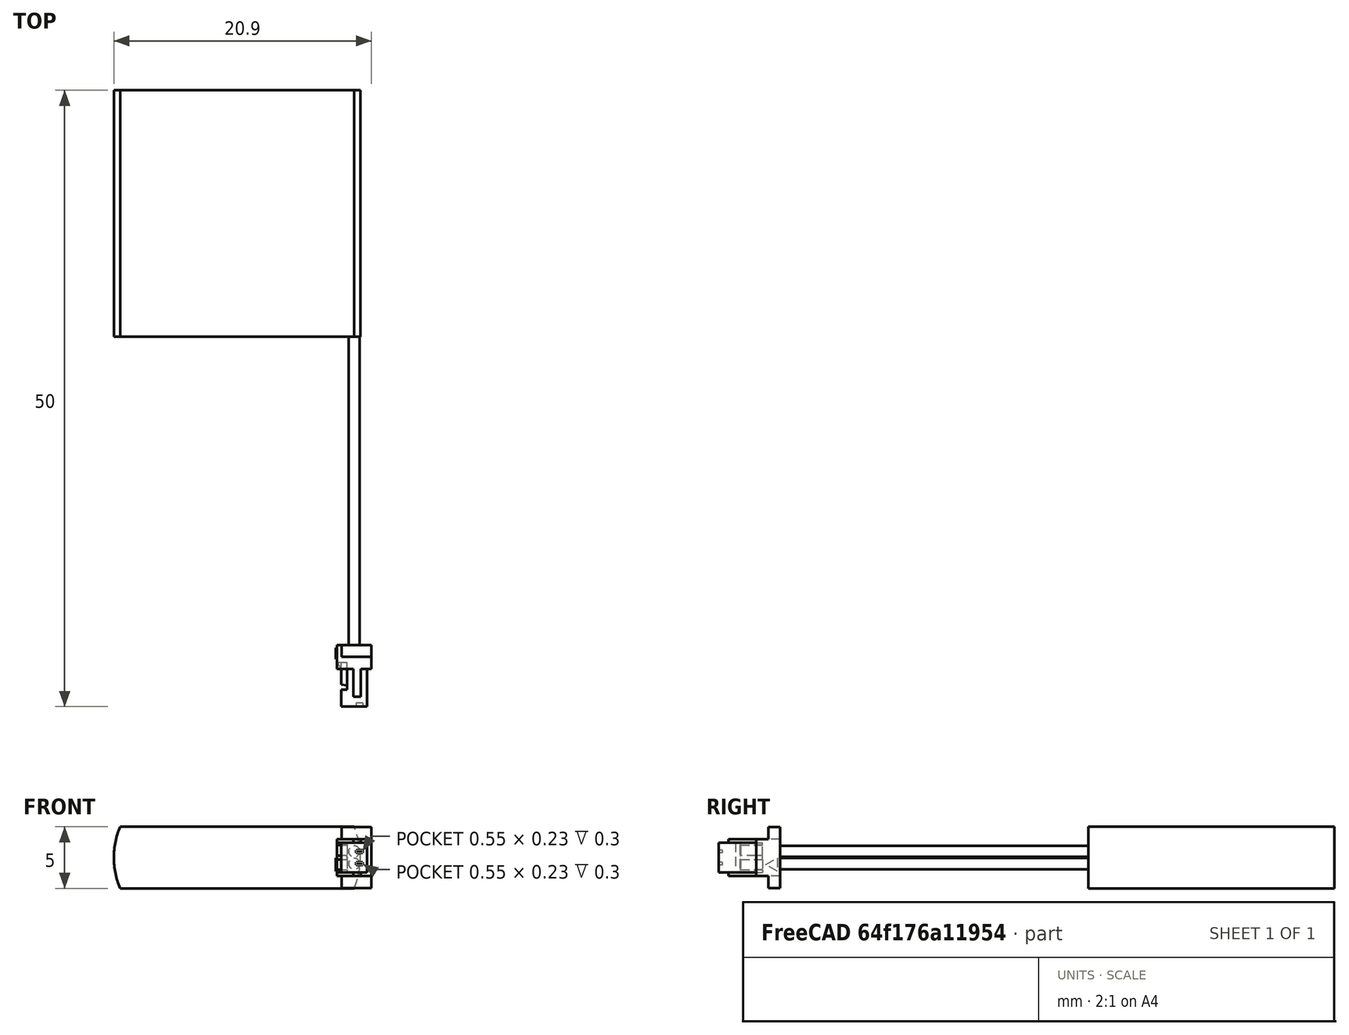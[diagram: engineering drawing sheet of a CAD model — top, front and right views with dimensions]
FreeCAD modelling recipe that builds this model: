
FCSTD DOCUMENT  (FreeCAD 2021.519R24301 +3652 (Git))
Label: ASR00003_150mAh
License: Other
objects: TechDraw::DrawViewDimension×4, Sketcher::SketchObject×3, PartDesign::Pad×3, TechDraw::DrawViewPart×2, TechDraw::DrawViewAnnotation×2, PartDesign::Pocket×1, PartDesign::Mirrored×1, PartDesign::Body×1, Part::Feature×1, Part::MultiFuse×1, TechDraw::DrawSVGTemplate×1, TechDraw::DrawPage×1, Mesh::Feature×1
note: 21 computed .brp shape members not serialized (recipe doc carries the construction recipe); baked Part::Feature solids carry a one-line shape summary decoded from their .brp

FEATURE [Sketcher::SketchObject] Sketch
  FullyConstrained = true
  MapMode = 5
  Support = -> [XY_Plane]
  sketch-geometry (4):
    g0: LineSegment StartX=-10 StartY=10 StartZ=0 EndX=10 EndY=10 EndZ=0
    g1: LineSegment StartX=10 StartY=10 StartZ=0 EndX=10 EndY=-10 EndZ=0
    g2: LineSegment StartX=10 StartY=-10 StartZ=0 EndX=-10 EndY=-10 EndZ=0
    g3: LineSegment StartX=-10 StartY=-10 StartZ=0 EndX=-10 EndY=10 EndZ=0
  constraints (10):
    c: Coincident(g0,g1)
    c: Coincident(g1,g2)
    c: Coincident(g2,g3)
    c: Coincident(g3,g0)
    c: Horizontal(g2)
    c: Vertical(g1)
    c: Symmetric(g0,g2,g-1)
    c: Symmetric(g0,g0,g-2)
    c: DistanceX(g0,g0) = 20
    c: DistanceY(g3,g3) = 20
FEATURE [PartDesign::Pad] Pad
  ClaimChildren = false
  Direction = (1,1,1)
  Fit = 0
  FitJoin = 0
  InnerFit = 0
  InnerFitJoin = 0
  InnerTaperAngle = 0
  InnerTaperAngleRev = 0
  Length = 5
  Length2 = 100
  Midplane = true
  NewSolid = false
  Profile = -> Sketch
  Suppress = false
  Type = 0
FEATURE [Sketcher::SketchObject] Sketch001
  ExternalGeometry = -> [Pad]
  FullyConstrained = true
  MapMode = 5
  Placement = pos=(0,10,0) rot=(0,0.707107,0.707107;3.14159rad)
  Support = -> [Pad]
  sketch-geometry (5):
    g0: ArcOfCircle CenterX=-3.5 CenterY=5e-16 CenterZ=0 NormalX=0 NormalY=0 NormalZ=1 AngleXU=0 Radius=6.5 StartAngle=2.7468 EndAngle=3.53638
    g1: LineSegment [constr] StartX=-9.5 StartY=-2.5 StartZ=0 EndX=-9.5 EndY=2.5 EndZ=0
    g2: LineSegment StartX=-9.5 StartY=-2.5 StartZ=0 EndX=-11 EndY=-2.5 EndZ=0
    g3: LineSegment StartX=-9.5 StartY=2.5 StartZ=0 EndX=-11 EndY=2.5 EndZ=0
    g4: LineSegment StartX=-11 StartY=2.5 StartZ=0 EndX=-11 EndY=-2.5 EndZ=0
  constraints (15):
    c: PointOnObject(g0,g-5)
    c: PointOnObject(g0,g-4)
    c: Tangent(g0,g-3)
    c: Coincident(g1,g0)
    c: Coincident(g1,g0)
    c: Vertical(g1)
    c: Coincident(g2,g0)
    c: Horizontal(g2)
    c: Coincident(g3,g0)
    c: Horizontal(g3)
    c: Coincident(g4,g3)
    c: Coincident(g4,g2)
    c: Vertical(g4)
    c: DistanceX(g3,g-4) = 1
    c: DistanceX(g-4,g0) = 0.5
FEATURE [PartDesign::Pocket] Pocket
  BaseFeature = -> Pad
  ClaimChildren = false
  Fit = 0
  FitJoin = 0
  InnerFit = 0
  InnerFitJoin = 0
  InnerTaperAngle = 0
  InnerTaperAngleRev = 0
  Length = 5
  Length2 = 100
  NewSolid = false
  Profile = -> Sketch001
  Suppress = false
  Type = 1
FEATURE [PartDesign::Mirrored] Mirrored
  BaseFeature = -> Pocket
  CopyShape = true
  MirrorPlane = -> Sketch001 [V_Axis]
  NewSolid = false
  OriginalSubs = -> [Pocket]
  Originals = -> [Pocket]
  ParallelTransform = true
  SubTransform = true
  Suppress = false
FEATURE [PartDesign::Pad] Pad001
  BaseFeature = -> Mirrored
  ClaimChildren = false
  Direction = (1,1,1)
  Fit = 0
  FitJoin = 0
  InnerFit = 0
  InnerFitJoin = 0
  InnerTaperAngle = 0
  InnerTaperAngleRev = 0
  Length = 7.85
  Length2 = 100
  NewSolid = false
  Profile = -> Mirrored [Face8]
  Reversed = true
  Suppress = false
  Type = 0
FEATURE [Sketcher::SketchObject] Sketch002
  ExternalGeometry = -> [Pad001]
  FullyConstrained = true
  MapMode = 5
  Placement = pos=(0,-10,0) rot=(1,0,0;1.5708rad)
  Support = -> [Pad001]
  sketch-geometry (7):
    g0: Circle CenterX=9.5 CenterY=-0.5 CenterZ=0 NormalX=0 NormalY=0 NormalZ=1 AngleXU=0 Radius=0.45
    g1: Circle CenterX=9.5 CenterY=0.5 CenterZ=0 NormalX=0 NormalY=0 NormalZ=1 AngleXU=0 Radius=0.45
    g2: LineSegment [constr] StartX=9.5 StartY=0.5 StartZ=0 EndX=9.5 EndY=-0.5 EndZ=0
    g3: GeomPoint [constr] X=9.5 Y=-0.95 Z=0
    g4: GeomPoint [constr] X=9.5 Y=0.95 Z=0
    g5: LineSegment [constr] StartX=9.05 StartY=-0.5 StartZ=0 EndX=9.95 EndY=-0.5 EndZ=0
    g6: GeomPoint [constr] X=9.5 Y=0.05 Z=0
  constraints (16):
    c: Coincident(g2,g1)
    c: Coincident(g2,g0)
    c: Equal(g0,g1)
    c: Diameter(g0) = 0.9
    c: Symmetric(g0,g1,g-1)
    c: PointOnObject(g3,g2)
    c: PointOnObject(g4,g1)
    c: Symmetric(g3,g4,g-1)
    c: PointOnObject(g5,g0)
    c: PointOnObject(g5,g0)
    c: Horizontal(g5)
    c: PointOnObject(g0,g5)
    c: PointOnObject(g6,g1)
    c: PointOnObject(g6,g2)
    c: DistanceY(g-4,g6) = 0.05
    c: DistanceX(g5,g-4) = 0.05
FEATURE [PartDesign::Pad] Pad002
  BaseFeature = -> Pad001
  ClaimChildren = false
  Direction = (1,1,1)
  Fit = 0
  FitJoin = 0
  InnerFit = 0
  InnerFitJoin = 0
  InnerTaperAngle = 0
  InnerTaperAngleRev = 0
  Length = 25
  Length2 = 100
  NewSolid = false
  Profile = -> Sketch002
  Suppress = false
  Type = 0
FEATURE [PartDesign::Body] Body
  AutoGroupSolids = false
  ExportMode = 0
  Group = -> [Sketch,Pad,Sketch001,Pocket,Mirrored,Pad001,Sketch002,Pad002]
  Origin = -> Origin
  Tip = -> Pad002
  _ExportChildren = -> [Pad,Pocket,Mirrored,Pad001,Pad002]
  _GroupVersion = 1
FEATURE [Part::Feature] Solid  label="Body007"
  Placement = pos=(8.21545,-37,6.7e-15) rot=(0,0,1;0rad)
  shape: bbox 2.9 x 5 x 4.94 mm, 60 faces (baked)
FEATURE [Part::MultiFuse] Fusion
  Shapes = -> [Body,Solid]
FEATURE [TechDraw::DrawSVGTemplate] Template
  Height = 210
  Orientation = 1
  Width = 297
FEATURE [TechDraw::DrawViewPart] View
  CoarseView = false
  Direction = (0,0,1)
  Focus = 100
  HardHidden = false
  IsoCount = 0
  IsoHidden = false
  IsoVisible = false
  LockPosition = false
  Perspective = false
  Rotation = 180
  Scale = 2.19
  ScaleType = 0
  SeamHidden = false
  SeamVisible = true
  SmoothHidden = false
  SmoothVisible = true
  Source = -> [Fusion]
  X = 178.5
  XDirection = (1,0,0)
  Y = 105
FEATURE [TechDraw::DrawViewPart] View001
  CoarseView = false
  Direction = (-1,0,0)
  Focus = 100
  HardHidden = false
  IsoCount = 0
  IsoHidden = false
  IsoVisible = false
  LockPosition = false
  Perspective = false
  Rotation = 90
  Scale = 2.19
  ScaleType = 0
  SeamHidden = false
  SeamVisible = true
  SmoothHidden = false
  SmoothVisible = true
  Source = -> [Fusion]
  X = 118.5
  XDirection = (0,-1,0)
  Y = 105
FEATURE [TechDraw::DrawViewAnnotation] Annotation
  Font = MS Shell Dlg 2
  LineSpace = 80
  LockPosition = false
  MaxWidth = -1
  Rotation = 0
  ScaleType = 0
  Text = SIDE VIEW
  TextSize = 6
  TextStyle = 0
  X = 118.5
  Y = 162
FEATURE [TechDraw::DrawViewAnnotation] Annotation001
  Font = MS Shell Dlg 2
  LineSpace = 80
  LockPosition = false
  MaxWidth = -1
  Rotation = 0
  ScaleType = 0
  Text = TOP VIEW
  TextSize = 6
  TextStyle = 0
  X = 178.5
  Y = 162
FEATURE [TechDraw::DrawViewDimension] Dimension
  Arbitrary = false
  ArbitraryTolerances = false
  EqualTolerance = true
  FormatSpec = %.1f
  FormatSpecOverTolerance = %+.1f
  FormatSpecUnderTolerance = %+.1f
  Inverted = false
  LockPosition = false
  MeasureType = 1
  OverTolerance = 0.5
  References2D = -> [View001]
  Rotation = 0
  ScaleType = 0
  TheoreticalExact = false
  Type = 1
  UnderTolerance = -0.5
  X = -34
  Y = -59
FEATURE [TechDraw::DrawViewDimension] Dimension001
  Arbitrary = false
  ArbitraryTolerances = false
  EqualTolerance = true
  FormatSpec = %.1f
  FormatSpecOverTolerance = %+.1f
  FormatSpecUnderTolerance = %+.1f
  Inverted = false
  LockPosition = false
  MeasureType = 1
  OverTolerance = 2
  References2D = -> [View]
  Rotation = 0
  ScaleType = 0
  TheoreticalExact = false
  Type = 1
  UnderTolerance = -2
  X = 40.9855
  Y = -59
FEATURE [TechDraw::DrawViewDimension] Dimension002
  Arbitrary = false
  ArbitraryTolerances = false
  EqualTolerance = true
  FormatSpec = %.1f
  FormatSpecOverTolerance = %+.1f
  FormatSpecUnderTolerance = %+.1f
  Inverted = false
  LockPosition = false
  MeasureType = 1
  OverTolerance = 3
  References2D = -> [View]
  Rotation = 0
  ScaleType = 0
  TheoreticalExact = false
  Type = 2
  UnderTolerance = -3
  X = -35
  Y = -31.6414
FEATURE [TechDraw::DrawViewDimension] Dimension003
  Arbitrary = false
  ArbitraryTolerances = false
  EqualTolerance = true
  FormatSpec = %.1f
  FormatSpecOverTolerance = %+.1f
  FormatSpecUnderTolerance = %+.1f
  Inverted = false
  LockPosition = false
  MeasureType = 1
  OverTolerance = 10
  References2D = -> [View]
  Rotation = 0
  ScaleType = 0
  TheoreticalExact = false
  Type = 2
  UnderTolerance = -10
  X = -35
  Y = 18
FEATURE [TechDraw::DrawPage] Page
  KeepUpdated = true
  NextBalloonIndex = 1
  ProjectionType = 0
  Template = -> Template
  Views = -> [View,View001,Annotation,Annotation001,Dimension,Dimension001,Dimension002,Dimension003]
FEATURE [Mesh::Feature] Mesh  label="Fusion (Meshed)"
